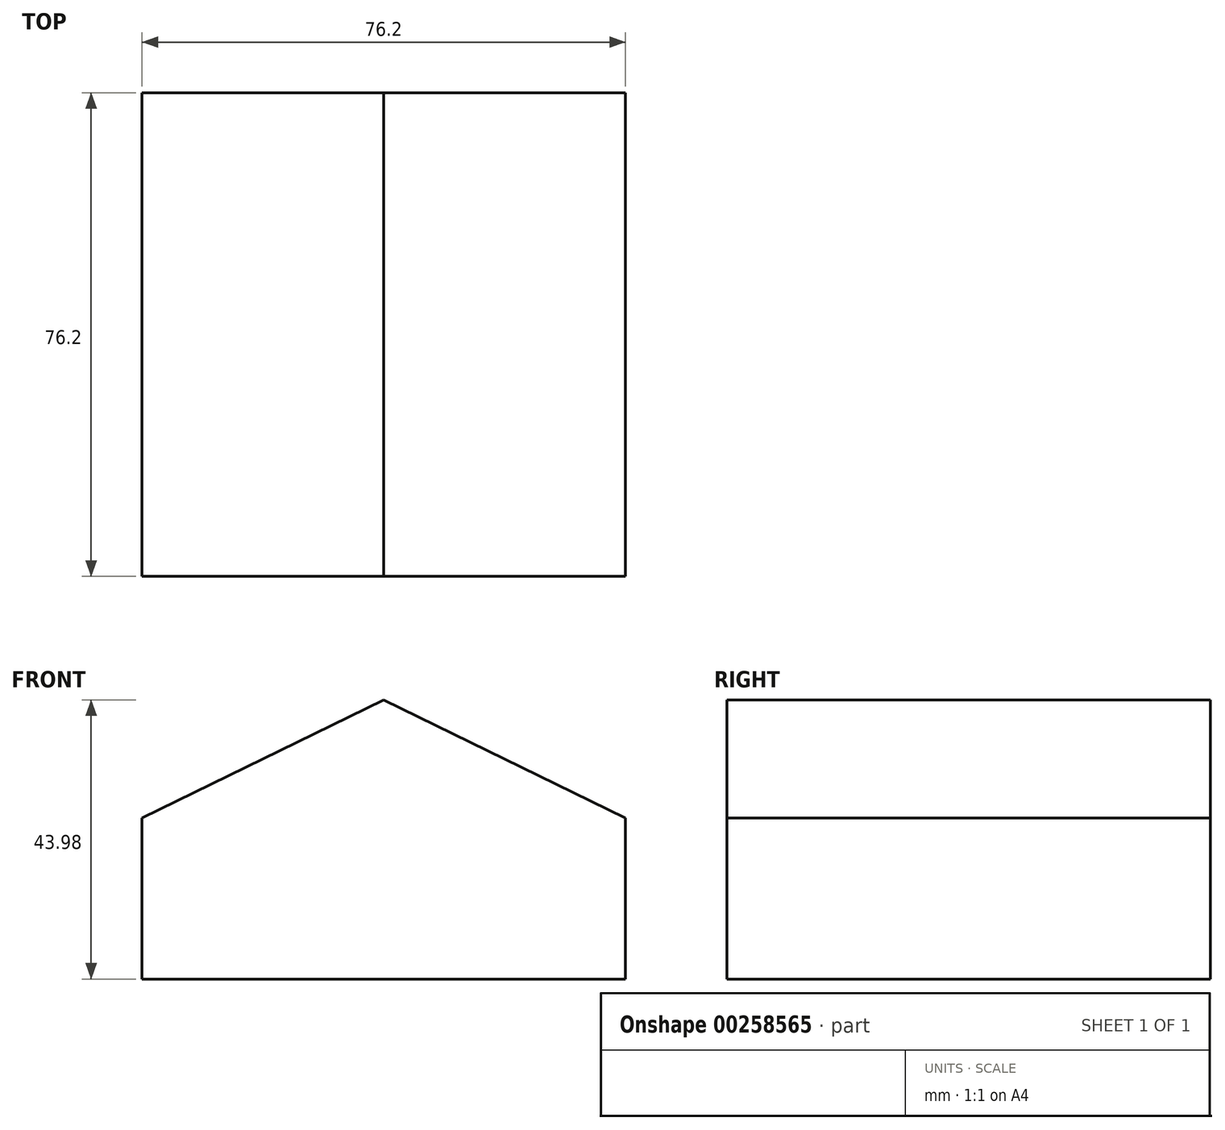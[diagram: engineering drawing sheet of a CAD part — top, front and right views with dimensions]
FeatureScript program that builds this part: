
annotation { "Feature Type Name" : "Feature", "Feature Type Description" : "" }
export const myFeature = defineFeature(function(context is Context, id is Id, definition is map)
    precondition{}
    {
        {
            var Q0;
            Q0=qCreatedBy(makeId("Top.planeOp"),FACE);
            var sketch = newSketch(context, id + "F0", { "sketchPlane" : qUnion([Q0])});
            skLineSegment(sketch, "E0.bottom", {"start": v(-43.55, 37.69) * mm, "end": v(32.65, 37.69) * mm});
            skLineSegment(sketch, "E0.top", {"start": v(-43.55, -38.51) * mm, "end": v(32.65, -38.51) * mm});
            skLineSegment(sketch, "E0.left", {"start": v(-43.55, 37.69) * mm, "end": v(-43.55, -38.51) * mm});
            skLineSegment(sketch, "E0.right", {"start": v(32.65, 37.69) * mm, "end": v(32.65, -38.51) * mm});
            skLineSegment(sketch, "E1", {"start": v(-43.55, 0) * mm, "end": v(32.65, 0) * mm});
            skSolve(sketch);
        }
        {
            var Q0;
            {var subQ0=sQuery(id+"F0.wireOp",EDGE,"E0.bottom");Q0=makeQuery(id+"F0.imprint","IMPRINT",FACE,{"disambiguationData":[TD([[makeQuery(id+"F0.imprint","IMPRINT",EDGE,{"derivedFrom":subQ0}),-1.0]])]});}
            var Q1;
            {var subQ0=sQuery(id+"F0.wireOp",EDGE,"E0.top");Q1=makeQuery(id+"F0.imprint","IMPRINT",FACE,{"disambiguationData":[TD([[makeQuery(id+"F0.imprint","IMPRINT",EDGE,{"derivedFrom":subQ0}),1.0]])]});}
            extrude(context, id + "F1", {"entities" : qUnion([Q0, Q1]), "depth" : 25.4 * mm});
        }
        {
            var Q0;
            Q0=makeQuery(id+"F1.opExtrude","SWEPT_FACE",FACE,{"disambiguationData":[OSD([sQuery(id+"F0.wireOp",EDGE,"E0.top")])]});
            var sketch = newSketch(context, id + "F2", { "sketchPlane" : qUnion([Q0])});
            skLineSegment(sketch, "E2", {"start": v(32.65, 25.4) * mm, "end": v(-43.55, 25.4) * mm});
            skLineSegment(sketch, "E3", {"start": v(-43.55, 25.4) * mm, "end": v(-5.45, 43.98) * mm});
            skPoint(sketch, "E3.endSnap0", {"position": v(-5.45, 25.4) * mm});
            skLineSegment(sketch, "E4", {"start": v(-5.45, 43.98) * mm, "end": v(32.65, 25.4) * mm});
            skPoint(sketch, "E5.orphan", {"position": v(0, 43.98) * mm});
            skSolve(sketch);
        }
        {
            var Q0;
            Q0=makeQuery(id+"F2.imprint","IMPRINT",FACE,{"disambiguationData":[TD([[makeQuery(id+"F2.imprint","IMPRINT",EDGE,{"derivedFrom":sQuery(id+"F2.wireOp",EDGE,"E2")}),1.0]])]});
            extrude(context, id + "F3", {"entities" : qUnion([Q0]), "operationType" : NewBodyOperationType.ADD, "oppositeDirection" : true, "depth" : 76.2 * mm});
        }
    });
